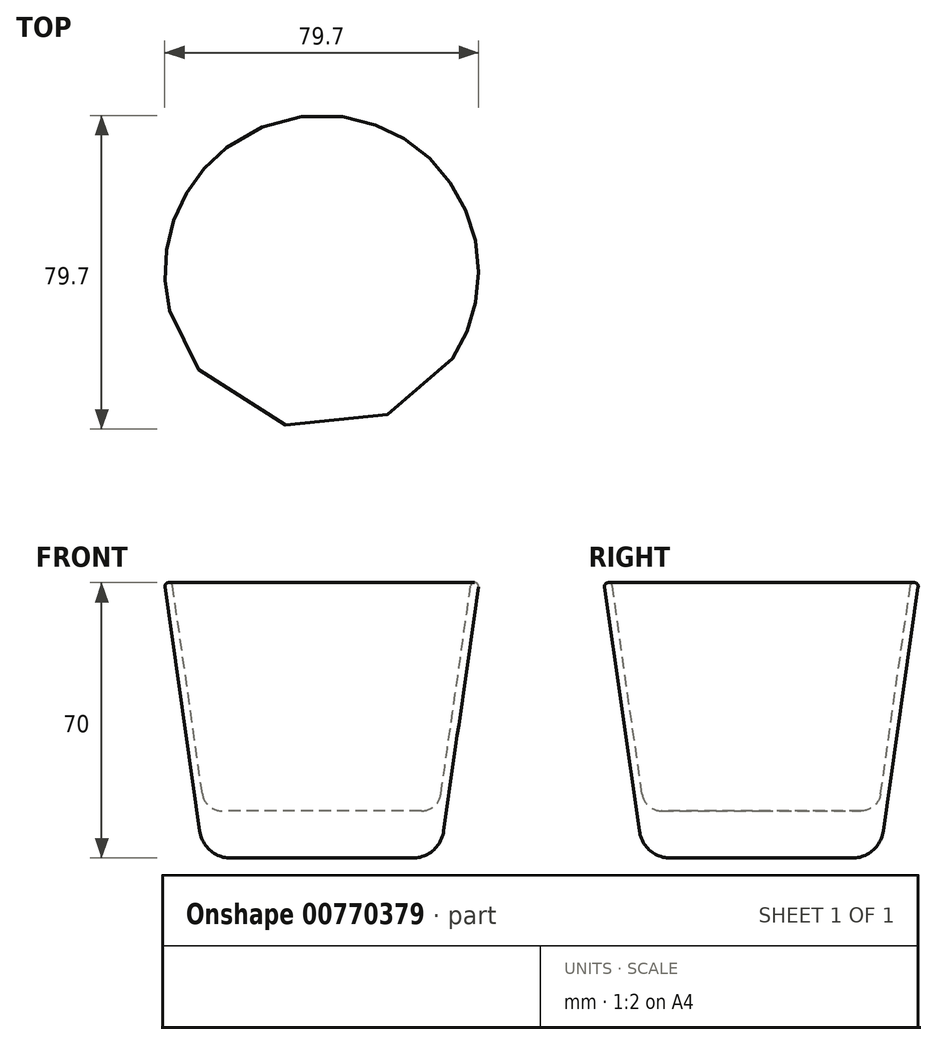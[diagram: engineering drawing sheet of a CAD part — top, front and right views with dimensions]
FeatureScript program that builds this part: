
annotation { "Feature Type Name" : "Feature", "Feature Type Description" : "" }
export const myFeature = defineFeature(function(context is Context, id is Id, definition is map)
    precondition{}
    {
        {
            var Q0;
            Q0=qCreatedBy(makeId("Front.planeOp"),FACE);
            var sketch = newSketch(context, id + "F0", { "sketchPlane" : qUnion([Q0])});
            skLineSegment(sketch, "E0", {"start": v(0, 0) * mm, "end": v(0, 102.03) * mm, "construction": true});
            skLineSegment(sketch, "E1", {"start": v(0, 0) * mm, "end": v(23.06, 0) * mm});
            skLineSegment(sketch, "E2", {"start": v(30.98, 6.87) * mm, "end": v(39.84, 68.86) * mm});
            skPoint(sketch, "E3.visualSharp", {"position": v(30, 0) * mm});
            skArc(sketch, "E3.filletArc", {"start": v(23.06, 0) * mm, "mid": v(28.3, 1.96) * mm, "end": v(30.98, 6.87) * mm});
            skLineSegment(sketch, "E4.0", {"start": v(30.3, 16.3) * mm, "end": v(37.86, 69.14) * mm});
            skLineSegment(sketch, "E5.0", {"start": v(0, 12) * mm, "end": v(25.36, 12) * mm});
            skArc(sketch, "E6.filletArc", {"start": v(25.36, 12) * mm, "mid": v(28.63, 13.22) * mm, "end": v(30.3, 16.3) * mm});
            skArc(sketch, "E7", {"start": v(39.84, 68.86) * mm, "mid": v(38.99, 69.99) * mm, "end": v(37.86, 69.14) * mm});
            skPoint(sketch, "E8.orphan", {"position": v(40, 70) * mm});
            skLineSegment(sketch, "E9", {"start": v(0, 12) * mm, "end": v(0, 0) * mm});
            skSolve(sketch);
        }
        {
            var Q0;
            Q0=makeQuery(id+"F0.imprint","IMPRINT",FACE,{"disambiguationData":[TD([[makeQuery(id+"F0.imprint","IMPRINT",EDGE,{"derivedFrom":sQuery(id+"F0.wireOp",EDGE,"E1")}),1.0]])]});
            var Q1;
            Q1=sQuery(id+"F0.wireOp",EDGE,"E9");
            revolve(context, id + "F1", {"surfaceOperationType" : NewSurfaceOperationType.NEW, "entities" : qUnion([Q0]), "axis" : qUnion([Q1]), "revolveType" : RevolveType.FULL});
        }
    });
